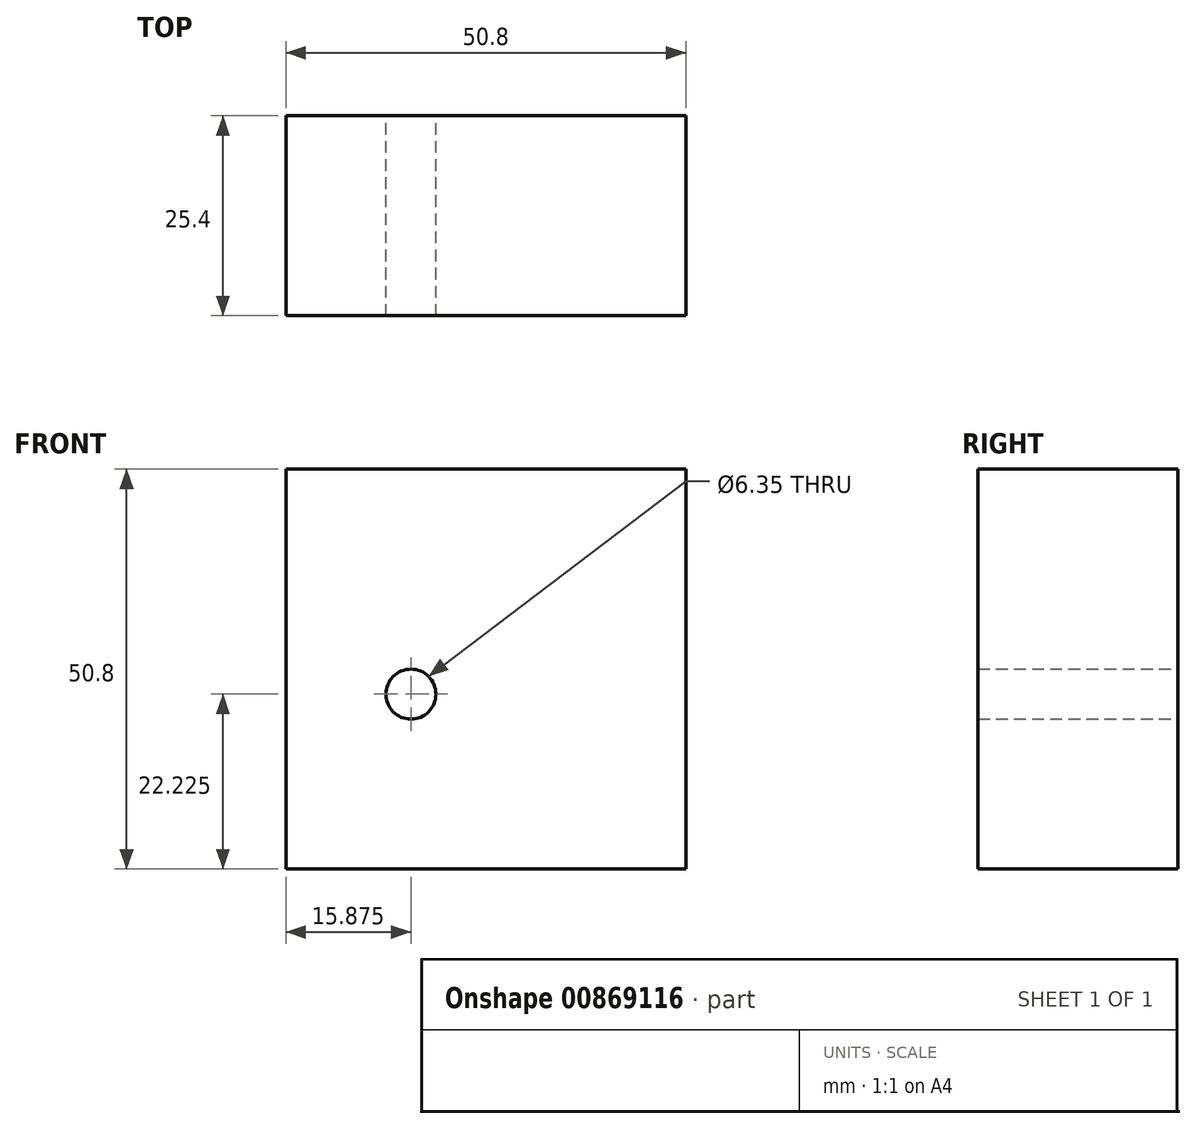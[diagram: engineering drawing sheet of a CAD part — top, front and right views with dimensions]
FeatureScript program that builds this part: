
annotation { "Feature Type Name" : "Feature", "Feature Type Description" : "" }
export const myFeature = defineFeature(function(context is Context, id is Id, definition is map)
    precondition{}
    {
        {
            var Q0;
            Q0=qCreatedBy(makeId("Front.planeOp"),FACE);
            var sketch = newSketch(context, id + "F0", { "sketchPlane" : qUnion([Q0])});
            skLineSegment(sketch, "E0.bottom", {"start": v(-50.8, 50.8) * mm, "end": v(0, 50.8) * mm});
            skLineSegment(sketch, "E0.top", {"start": v(-50.8, 0) * mm, "end": v(0, 0) * mm});
            skLineSegment(sketch, "E0.left", {"start": v(-50.8, 50.8) * mm, "end": v(-50.8, 0) * mm});
            skLineSegment(sketch, "E0.right", {"start": v(0, 50.8) * mm, "end": v(0, 0) * mm});
            skCircle(sketch, "E1", {"center": v(-34.93, 22.23) * mm, "radius": 3.18 * mm});
            skSolve(sketch);
        }
        {
            var Q0;
            Q0 = qSketchRegion(id + "F0", true);
            extrude(context, id + "F1", {"entities" : qUnion([Q0]), "depth" : 25.4 * mm, "offsetDistance" : 25.4 * mm});
        }
    });
